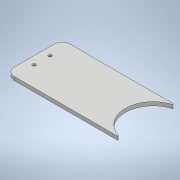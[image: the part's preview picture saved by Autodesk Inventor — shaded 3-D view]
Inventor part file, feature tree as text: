
AUTODESK INVENTOR PART (.ipt)
format: ipt  version: 2020 (Build 240168000, 168)  size: 127,488 bytes
history: native  units: mm
features: fillet x2, extrude x1, hole x1, sketch x1
ambient origin geometry x8: Origin, YZ Plane, XZ Plane, XY Plane, X Axis, Y Axis, Z Axis, Center Point
bodies: Body1 (feature_tree)
feature tree (5):
  extrude  "Выдавливание3"  Depth=12.25mm
  fillet  "Сопряжение3"  Radius=1.6mm
  fillet  "Сопряжение4"  Radius=40.0mm
  hole  "Отверстие1"  [1 undecoded]
  sketch  "Эскиз6"
note: 1 required parameter value undecoded (feature->parameter linkage not recoverable at this tier; creation-order binding heuristic only, values carry confidence <= 0.55)
